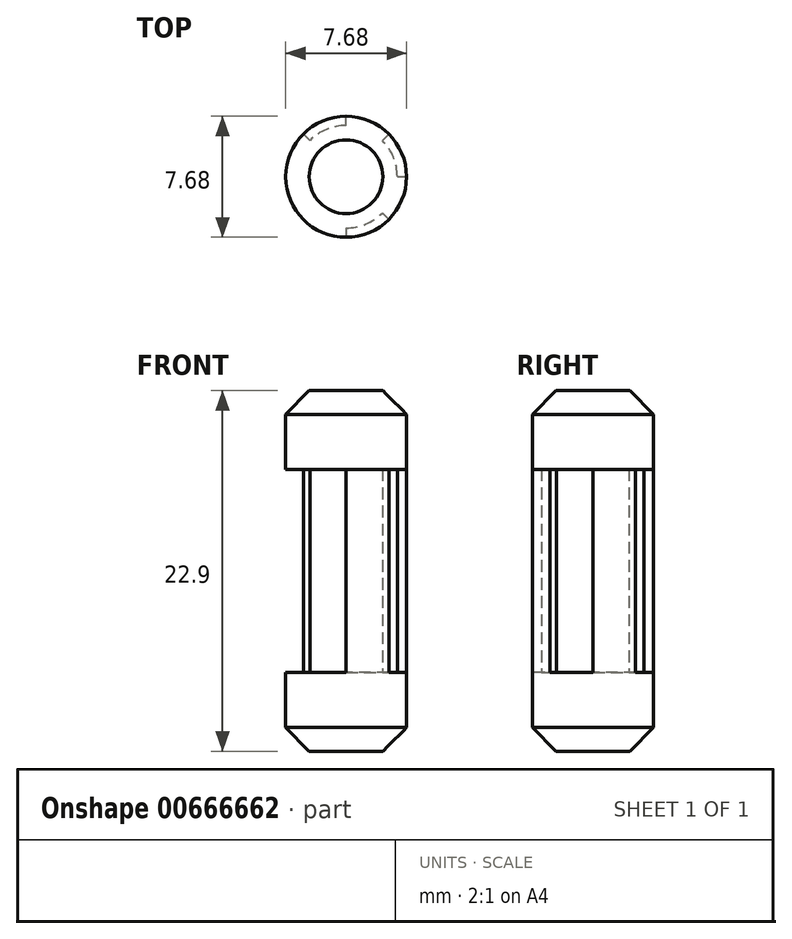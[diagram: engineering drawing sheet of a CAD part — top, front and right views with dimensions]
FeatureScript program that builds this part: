
annotation { "Feature Type Name" : "Feature", "Feature Type Description" : "" }
export const myFeature = defineFeature(function(context is Context, id is Id, definition is map)
    precondition{}
    {
        {
            var Q0;
            Q0=qCreatedBy(makeId("Top.planeOp"),FACE);
            var sketch = newSketch(context, id + "F0", { "sketchPlane" : qUnion([Q0])});
            skCircle(sketch, "E0", {"center": v(0, 0) * mm, "radius": 7.68 * mm});
            skSolve(sketch);
        }
        {
            var Q0;
            Q0=makeQuery(id+"F0.imprint","IMPRINT",FACE,{"disambiguationData":[TD([[makeQuery(id+"F0.imprint","IMPRINT",EDGE,{"derivedFrom":sQuery(id+"F0.wireOp",EDGE,"E0")}),1.0]])]});
            extrude(context, id + "F1", {"entities" : qUnion([Q0]), "depth" : 10 * mm, "offsetDistance" : 25 * mm});
        }
        {
            var Q0;
            Q0=makeQuery(id+"F1.opExtrude","CAP_FACE",FACE,{"disambiguationData":[OSD([sQuery(id+"F0.wireOp",EDGE,"E0")])],"isStart":false});
            var sketch = newSketch(context, id + "F2", { "sketchPlane" : qUnion([Q0])});
            skLineSegment(sketch, "E1", {"start": v(0, 0) * mm, "end": v(-7.68, 0) * mm});
            skLineSegment(sketch, "E2", {"start": v(-7.68, 0) * mm, "end": v(7.68, 0) * mm});
            skLineSegment(sketch, "E3", {"start": v(0, 0) * mm, "end": v(0, -7.68) * mm});
            skLineSegment(sketch, "E4", {"start": v(0, 0) * mm, "end": v(0, 7.68) * mm});
            skLineSegment(sketch, "E5", {"start": v(-4.6, 4.6) * mm, "end": v(5.43, -5.43) * mm});
            skLineSegment(sketch, "E6", {"start": v(5.43, -5.43) * mm, "end": v(-5.43, 5.43) * mm});
            skLineSegment(sketch, "E7", {"start": v(-3.84, -3.84) * mm, "end": v(5.43, 5.43) * mm});
            skLineSegment(sketch, "E8", {"start": v(5.43, 5.43) * mm, "end": v(-5.43, -5.43) * mm});
            skCircle(sketch, "E9", {"center": v(0, 0) * mm, "radius": 6.51 * mm});
            skSolve(sketch);
        }
        {
            var Q0;
            {var subQ0=sQuery(id+"F2.wireOp",EDGE,"E3");var subQ1=makeQuery(id+"F1.opExtrude","CAP_EDGE",EDGE,{"disambiguationData":[OSD([sQuery(id+"F0.wireOp",EDGE,"E0")])],"isStart":false});var subQ2=makeQuery(id+"F2.imprint","INTERSECT",VERTEX,{"derivedFrom":[subQ1,subQ0]});Q0=makeQuery(id+"F2.imprint","IMPRINT",FACE,{"disambiguationData":[TD([[makeQuery(id+"F2.imprint","IMPRINT",EDGE,{"disambiguationData":[TD([[subQ2,1.0]])],"derivedFrom":subQ0}),1.0]])]});}
            var Q1;
            {var subQ0=sQuery(id+"F2.wireOp",EDGE,"E2");var subQ1=makeQuery(id+"F1.opExtrude","CAP_EDGE",EDGE,{"disambiguationData":[OSD([sQuery(id+"F0.wireOp",EDGE,"E0")])],"isStart":false});var subQ2=makeQuery(id+"F2.imprint","INTERSECT",VERTEX,{"disambiguationData":[OD(1.0)],"derivedFrom":[subQ1,subQ0]});Q1=makeQuery(id+"F2.imprint","IMPRINT",FACE,{"disambiguationData":[TD([[makeQuery(id+"F2.imprint","IMPRINT",EDGE,{"disambiguationData":[TD([[subQ2,1.0]])],"derivedFrom":subQ0}),1.0]])]});}
            var Q2;
            {var subQ0=sQuery(id+"F2.wireOp",EDGE,"E4");var subQ1=makeQuery(id+"F1.opExtrude","CAP_EDGE",EDGE,{"disambiguationData":[OSD([sQuery(id+"F0.wireOp",EDGE,"E0")])],"isStart":false});var subQ2=makeQuery(id+"F2.imprint","INTERSECT",VERTEX,{"derivedFrom":[subQ1,subQ0]});Q2=makeQuery(id+"F2.imprint","IMPRINT",FACE,{"disambiguationData":[TD([[makeQuery(id+"F2.imprint","IMPRINT",EDGE,{"disambiguationData":[TD([[subQ2,1.0]])],"derivedFrom":subQ0}),1.0]])]});}
            var Q3;
            {var subQ0=sQuery(id+"F2.wireOp",EDGE,"E2");var subQ1=makeQuery(id+"F1.opExtrude","CAP_EDGE",EDGE,{"disambiguationData":[OSD([sQuery(id+"F0.wireOp",EDGE,"E0")])],"isStart":false});var subQ2=makeQuery(id+"F2.imprint","INTERSECT",VERTEX,{"disambiguationData":[OD(0.0)],"derivedFrom":[subQ1,subQ0]});Q3=makeQuery(id+"F2.imprint","IMPRINT",FACE,{"disambiguationData":[TD([[makeQuery(id+"F2.imprint","IMPRINT",EDGE,{"disambiguationData":[TD([[subQ2,-1.0]])],"derivedFrom":subQ0}),-1.0]])]});}
            extrude(context, id + "F3", {"entities" : qUnion([Q0, Q1, Q2, Q3]), "operationType" : NewBodyOperationType.ADD, "depth" : 25.8 * mm, "offsetDistance" : 25 * mm});
        }
        {
            var Q0;
            {var subQ0=sQuery(id+"F2.wireOp",EDGE,"E2");var subQ1=sQuery(id+"F0.wireOp",EDGE,"E0");var subQ2=makeQuery(id+"F1.opExtrude","CAP_EDGE",EDGE,{"disambiguationData":[OSD([subQ1])],"isStart":false});var subQ3=makeQuery(id+"F2.imprint","INTERSECT",VERTEX,{"disambiguationData":[OD(1.0)],"derivedFrom":[subQ2,subQ0]});var subQ4=sQuery(id+"F2.wireOp",EDGE,"E8");var subQ5=makeQuery(id+"F2.imprint","INTERSECT",VERTEX,{"disambiguationData":[OD(0.0)],"derivedFrom":[subQ2,subQ4]});var subQ6=sQuery(id+"F2.wireOp",EDGE,"E9");var subQ7=makeQuery(id+"F2.imprint","INTERSECT",VERTEX,{"disambiguationData":[OD(1.0)],"derivedFrom":[subQ0,subQ6]});Q0=makeQuery(id+"F3.opExtrude","CAP_FACE",FACE,{"disambiguationData":[OSD([subQ1,subQ0,subQ4,subQ6]),TDD([makeQuery(id+"F2.imprint","IMPRINT",EDGE,{"disambiguationData":[TD([[subQ3,1.0]])],"derivedFrom":subQ0}),makeQuery(id+"F2.imprint","IMPRINT",EDGE,{"disambiguationData":[TD([[subQ5,-1.0]])],"derivedFrom":subQ4}),makeQuery(id+"F2.imprint","IMPRINT",EDGE,{"disambiguationData":[TD([[subQ7,-1.0]])],"derivedFrom":subQ6}),makeQuery(id+"F2.imprint","IMPRINT",EDGE,{"disambiguationData":[TD([[subQ3,-1.0]])],"derivedFrom":subQ2})])],"isStart":false});}
            var sketch = newSketch(context, id + "F4", { "sketchPlane" : qUnion([Q0])});
            skCircle(sketch, "E10", {"center": v(0, 0) * mm, "radius": 7.68 * mm});
            skSolve(sketch);
        }
        {
            var Q0;
            Q0 = qSketchRegion(id + "F4", true);
            extrude(context, id + "F5", {"entities" : qUnion([Q0]), "depth" : 10 * mm, "offsetDistance" : 25 * mm});
        }
        {
            var Q0;
            Q0=makeQuery(id+"F1.opExtrude","CAP_EDGE",EDGE,{"disambiguationData":[OSD([sQuery(id+"F0.wireOp",EDGE,"E0")])],"isStart":true});
            var Q1;
            Q1=makeQuery(id+"F5.opExtrude","CAP_EDGE",EDGE,{"disambiguationData":[OSD([sQuery(id+"F4.wireOp",EDGE,"E10")])],"isStart":false});
            chamfer(context, id + "F6", {"entities" : qUnion([Q0, Q1]), "width" : 3 * mm, "tangentPropagation" : true});
        }
        {
            var Q0;
            Q0=makeQuery(id+"F1.opExtrude","SWEPT_BODY",BODY,{"disambiguationData":[OSD([sQuery(id+"F0.wireOp",EDGE,"E0")])]});
            var Q1;
            Q1=makeQuery(id+"F5.opExtrude","SWEPT_BODY",BODY,{"disambiguationData":[OSD([sQuery(id+"F4.wireOp",EDGE,"E10")])]});
            var Q2;
            Q2=qCreatedBy(makeId("Origin.pointOp"),VERTEX);
            transform(context, id + "F7", {"entities" : qUnion([Q0, Q1]), "transformType" : TransformType.SCALE_UNIFORMLY, "scale" : 0.5, "scalePoint" : qUnion([Q2]), "makeCopy" : false});
        }
    });
